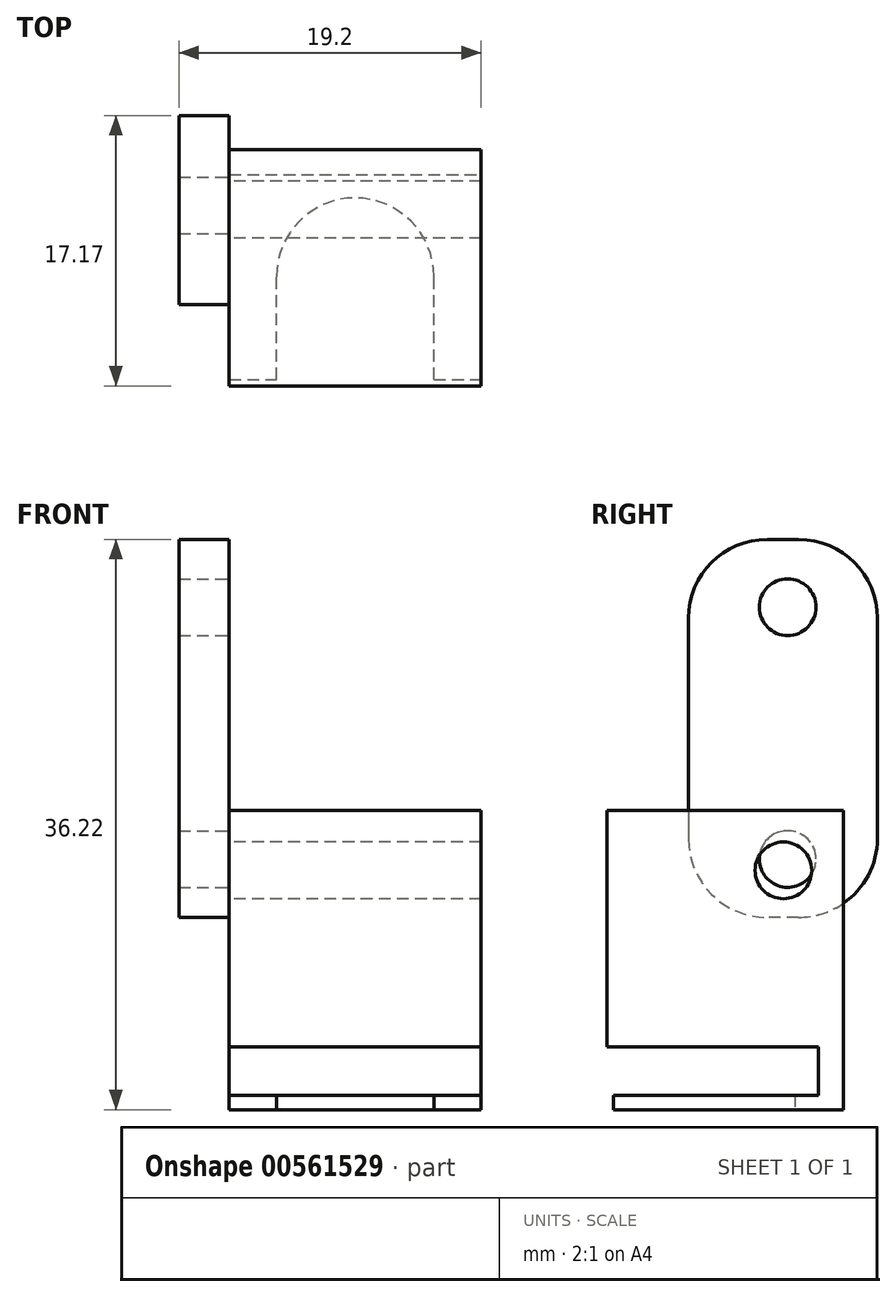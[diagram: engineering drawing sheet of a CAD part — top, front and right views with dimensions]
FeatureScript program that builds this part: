
annotation { "Feature Type Name" : "Feature", "Feature Type Description" : "" }
export const myFeature = defineFeature(function(context is Context, id is Id, definition is map)
    precondition{}
    {
        {
            var Q0;
            Q0=qCreatedBy(makeId("Front.planeOp"),FACE);
            var sketch = newSketch(context, id + "F0", { "sketchPlane" : qUnion([Q0])});
            skLineSegment(sketch, "E0.bottom", {"start": v(0, 15) * mm, "end": v(16, 15) * mm});
            skLineSegment(sketch, "E0.top", {"start": v(0, 0) * mm, "end": v(16, 0) * mm});
            skLineSegment(sketch, "E0.left", {"start": v(0, 15) * mm, "end": v(0, 0) * mm});
            skLineSegment(sketch, "E0.right", {"start": v(16, 15) * mm, "end": v(16, 0) * mm});
            skSolve(sketch);
        }
        {
            var Q0;
            Q0=makeQuery(id+"F0.imprint","IMPRINT",FACE,{"disambiguationData":[TD([[makeQuery(id+"F0.imprint","IMPRINT",EDGE,{"derivedFrom":sQuery(id+"F0.wireOp",EDGE,"E0.bottom")}),-1.0]])]});
            extrude(context, id + "F1", {"entities" : qUnion([Q0]), "depth" : 15 * mm, "offsetDistance" : 25 * mm});
        }
        {
            var Q0;
            Q0=makeQuery(id+"F1.opExtrude","SWEPT_FACE",FACE,{"disambiguationData":[OSD([sQuery(id+"F0.wireOp",EDGE,"E0.left")])]});
            var sketch = newSketch(context, id + "F2", { "sketchPlane" : qUnion([Q0])});
            skCircle(sketch, "E1", {"center": v(3.8, 11.2) * mm, "radius": 1.8 * mm});
            skSolve(sketch);
        }
        {
            var Q0;
            Q0=makeQuery(id+"F2.imprint","IMPRINT",FACE,{"disambiguationData":[TD([[makeQuery(id+"F2.imprint","IMPRINT",EDGE,{"derivedFrom":sQuery(id+"F2.wireOp",EDGE,"E1")}),1.0]])]});
            extrude(context, id + "F3", {"entities" : qUnion([Q0]), "operationType" : NewBodyOperationType.REMOVE, "oppositeDirection" : true, "depth" : 25 * mm, "offsetDistance" : 25 * mm});
        }
        {
            var Q0;
            Q0=makeQuery(id+"F1.opExtrude","SWEPT_FACE",FACE,{"disambiguationData":[OSD([sQuery(id+"F0.wireOp",EDGE,"E0.left")])]});
            var sketch = newSketch(context, id + "F4", { "sketchPlane" : qUnion([Q0])});
            skLineSegment(sketch, "E2.bottom", {"start": v(-2.17, 32.22) * mm, "end": v(9.83, 32.22) * mm});
            skLineSegment(sketch, "E2.top", {"start": v(-2.17, 8.22) * mm, "end": v(9.83, 8.22) * mm});
            skLineSegment(sketch, "E2.left", {"start": v(-2.17, 32.22) * mm, "end": v(-2.17, 8.22) * mm});
            skLineSegment(sketch, "E2.right", {"start": v(9.83, 32.22) * mm, "end": v(9.83, 8.22) * mm});
            skCircle(sketch, "E3", {"center": v(3.53, 27.92) * mm, "radius": 1.8 * mm});
            skCircle(sketch, "E4", {"center": v(3.53, 11.92) * mm, "radius": 1.8 * mm});
            skSolve(sketch);
        }
        {
            var Q0;
            Q0 = qSketchRegion(id + "F4", true);
            extrude(context, id + "F5", {"entities" : qUnion([Q0]), "depth" : 3.2 * mm, "offsetDistance" : 25 * mm});
        }
        {
            var Q0;
            Q0=makeQuery(id+"F5.opExtrude","SWEPT_EDGE",EDGE,{"disambiguationData":[OSD([sQuery(id+"F4.wireOp",EDGE,"E2.bottom"),sQuery(id+"F4.wireOp",EDGE,"E2.left")])]});
            var Q1;
            Q1=makeQuery(id+"F5.opExtrude","SWEPT_EDGE",EDGE,{"disambiguationData":[OSD([sQuery(id+"F4.wireOp",EDGE,"E2.bottom"),sQuery(id+"F4.wireOp",EDGE,"E2.right")])]});
            var Q2;
            Q2=makeQuery(id+"F5.opExtrude","SWEPT_EDGE",EDGE,{"disambiguationData":[OSD([sQuery(id+"F4.wireOp",EDGE,"E2.top"),sQuery(id+"F4.wireOp",EDGE,"E2.right")])]});
            var Q3;
            Q3=makeQuery(id+"F5.opExtrude","SWEPT_EDGE",EDGE,{"disambiguationData":[OSD([sQuery(id+"F4.wireOp",EDGE,"E2.top"),sQuery(id+"F4.wireOp",EDGE,"E2.left")])]});
            fillet(context, id + "F6", {"entities" : qUnion([Q0, Q1, Q2, Q3]), "radius" : 5 * mm, "tangentPropagation" : true, "allowEdgeOverflow" : false});
        }
        {
            var Q0;
            Q0=makeQuery(id+"F1.opExtrude","SWEPT_FACE",FACE,{"disambiguationData":[OSD([sQuery(id+"F0.wireOp",EDGE,"E0.top")])]});
            var sketch = newSketch(context, id + "F7", { "sketchPlane" : qUnion([Q0])});
            skLineSegment(sketch, "E5", {"start": v(0, 1.59) * mm, "end": v(16, 1.59) * mm});
            skLineSegment(sketch, "E6", {"start": v(16, 1.59) * mm, "end": v(16, 0) * mm});
            skLineSegment(sketch, "E7", {"start": v(16, 0) * mm, "end": v(0, 0) * mm});
            skLineSegment(sketch, "E8", {"start": v(0, 0) * mm, "end": v(0, 1.59) * mm});
            skSolve(sketch);
        }
        {
            var Q0;
            Q0 = qSketchRegion(id + "F7", true);
            extrude(context, id + "F8", {"entities" : qUnion([Q0]), "operationType" : NewBodyOperationType.ADD, "depth" : 4 * mm, "offsetDistance" : 25 * mm});
        }
        {
            var Q0;
            Q0=makeQuery(id+"F8.opExtrude","SWEPT_FACE",FACE,{"disambiguationData":[OSD([sQuery(id+"F7.wireOp",EDGE,"E5")])]});
            var sketch = newSketch(context, id + "F9", { "sketchPlane" : qUnion([Q0])});
            skLineSegment(sketch, "E9", {"start": v(0, -4) * mm, "end": v(0, -3.08) * mm});
            skLineSegment(sketch, "E10", {"start": v(0, -3.08) * mm, "end": v(16, -3.08) * mm});
            skLineSegment(sketch, "E11", {"start": v(16, -3.08) * mm, "end": v(16, -4) * mm});
            skLineSegment(sketch, "E12", {"start": v(16, -4) * mm, "end": v(0, -4) * mm});
            skSolve(sketch);
        }
        {
            var Q0;
            Q0 = qSketchRegion(id + "F9", true);
            extrude(context, id + "F10", {"entities" : qUnion([Q0]), "operationType" : NewBodyOperationType.ADD, "depth" : 13 * mm, "offsetDistance" : 25 * mm});
        }
        {
            var Q0;
            Q0=makeQuery(id+"F10.boolean.opBoolean","MERGE",FACE,{"derivedFrom":[makeQuery(id+"F8.opExtrude","CAP_FACE",FACE,{"disambiguationData":[OSD([sQuery(id+"F7.wireOp",EDGE,"E5"),sQuery(id+"F7.wireOp",EDGE,"E6"),sQuery(id+"F7.wireOp",EDGE,"E7"),sQuery(id+"F7.wireOp",EDGE,"E8")])],"isStart":false}),makeQuery(id+"F10.opExtrude","SWEPT_FACE",FACE,{"disambiguationData":[OSD([sQuery(id+"F9.wireOp",EDGE,"E12")])]})]});
            var sketch = newSketch(context, id + "F11", { "sketchPlane" : qUnion([Q0])});
            skLineSegment(sketch, "E13", {"start": v(3, 14.59) * mm, "end": v(3, 8.06) * mm});
            skLineSegment(sketch, "E14", {"start": v(13, 14.59) * mm, "end": v(13, 8.06) * mm});
            skLineSegment(sketch, "E15", {"start": v(13, 14.59) * mm, "end": v(3, 14.59) * mm});
            skArc(sketch, "E16", {"start": v(3, 8.06) * mm, "mid": v(8, 3.06) * mm, "end": v(13, 8.06) * mm});
            skSolve(sketch);
        }
        {
            var Q0;
            Q0 = qSketchRegion(id + "F11", true);
            extrude(context, id + "F12", {"entities" : qUnion([Q0]), "operationType" : NewBodyOperationType.REMOVE, "oppositeDirection" : true, "depth" : 2 * mm, "offsetDistance" : 25 * mm});
        }
    });
